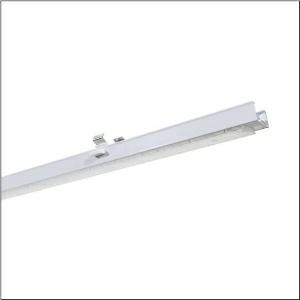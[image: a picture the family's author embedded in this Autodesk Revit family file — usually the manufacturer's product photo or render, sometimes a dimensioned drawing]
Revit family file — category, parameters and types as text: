
# Revit family: trunking_flex_31_51re19mb4cb
name_source: partatom
category: Lighting Fixtures
units: mm (PartAtom-declared; Revit-internal decimal feet)

## family parameters
Cut with Voids When Loaded = No
Host = Face
Light Source = No
Part Type = Normal
Room Calculation Point = No
Round Connector Dimension = Use Diameter
Shared = No

## types (1)
- --- (1 x LED, 11500 lm, 66 W, 4000K)
    Apparent Load = 66 VA
    CIE Flux Codes = 66 89 98 99 100
    Color Rendering = 80
    Color Temperature = 4000K
    Default Elevation = 1800 mm
    Description = Trunking Flex 31, luminaire insert, of extruded aluminium section, coated, traffic white (RAL 9016), length: 1.472mm, width: 91mm, height: 53mm, LED rated luminous flux: 11.500lm, light colour: 840, control gear: ON/OFF Multilumen, with system connector: socket, mains connection: 220..240V, AC, 50/60Hz, rated input power: 66W, connected load according to luminous flux setting (19/24/32/37/47/52/60/66W), luminous flux adjustable on luminaire in eight steps (3450/4380/5800/6700/8350/9200/10500/11500lm ), primary light control with lens, of plastic, primary optical cover: cover, of PMMA, light emission: direct distribution, primary light characteristic: double asymmetric, protection rating (complete): IP20, insulation class (complete): insulation class I (protective earthing), certification: CE, UKCA, impact resistance: IK02, permissible ambient temperature for indoor applications: -20..+40°C, packaging unit: 1 piece
    Height = 58 mm
    Lamp = 1 x LED
    Lamp Light Flux = 11500 lm
    Lamp Power = 66 W
    Lamp count = 1
    Length = 1472 mm
    Luminous efficacy = 174 lm/W
    Manufacturer = Siteco
    ModVariant = No
    Model = 51RE19MB4CB
    Mounting Place = Ceiling
    Mounting Type = Pendant
    Number of Poles = 1
    OnlyDefault = Yes
    Power Factor = 1
    Product Name = Trunking Flex 31
    Product group = luminaire insert | ceiling pendant
    ProductGroupID = 902
    Protection Class = Protection class I
    Protection Degree = IP 20
    RLX_Detail_Level = 1
    RLX_Emergency_Light_Flux = 0 lm
    RLX_Emergency_Type = 0
    RLX_Emergency_Type_DB = No
    RlxData = <blob elided: 21201 chars, md5=7a52928f>
    Socket = socket
    Standby Power = 0 W
    System Light Flux = 11500 lm
    System Power = 66 W
    Type Comments = factory setting: luminous flux: 100 % | (ON | ON | ON)
    Type Image = l_1266702.jpg
    URL = http://relux.com
    VarID = @adj_079295
    Voltage = 0 V
    Weight = 0.00 kg
    Width = 65 mm

## geometry (parser evidence)
native form markers: Blend x4, Sweep x13
no freeform markers — native parametric forms only
